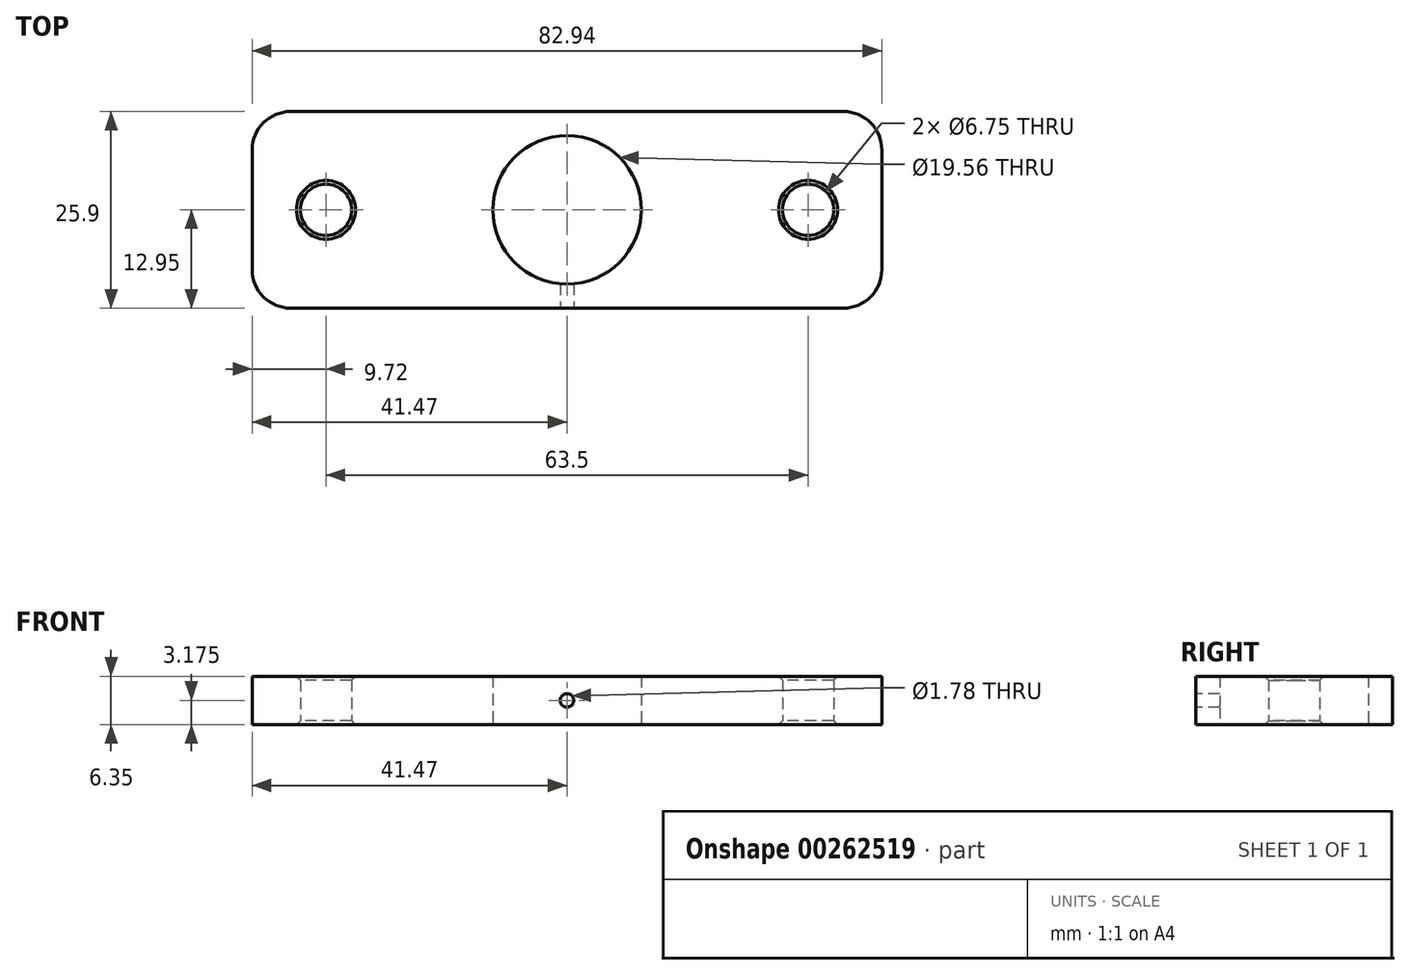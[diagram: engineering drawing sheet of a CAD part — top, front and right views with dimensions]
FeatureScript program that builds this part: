
annotation { "Feature Type Name" : "Feature", "Feature Type Description" : "" }
export const myFeature = defineFeature(function(context is Context, id is Id, definition is map)
    precondition{}
    {
        {
            var Q0;
            Q0=qCreatedBy(makeId("Top.planeOp"),FACE);
            var sketch = newSketch(context, id + "F0", { "sketchPlane" : qUnion([Q0])});
            skLineSegment(sketch, "E0.bottom", {"start": v(-41.47, 12.95) * mm, "end": v(41.47, 12.95) * mm});
            skLineSegment(sketch, "E0.top", {"start": v(-41.47, -12.95) * mm, "end": v(41.47, -12.95) * mm});
            skLineSegment(sketch, "E0.left", {"start": v(-41.47, 12.95) * mm, "end": v(-41.47, -12.95) * mm});
            skLineSegment(sketch, "E0.right", {"start": v(41.47, 12.95) * mm, "end": v(41.47, -12.95) * mm});
            skPoint(sketch, "E0.middle", {"position": v(0, 0) * mm});
            skCircle(sketch, "E1", {"center": v(0, 0) * mm, "radius": 9.78 * mm});
            skCircle(sketch, "E2", {"center": v(-31.75, 0) * mm, "radius": 3.37 * mm});
            skCircle(sketch, "E3", {"center": v(31.75, 0) * mm, "radius": 3.37 * mm});
            skSolve(sketch);
        }
        {
            var Q0;
            Q0 = qSketchRegion(id + "F0", true);
            extrude(context, id + "F1", {"entities" : qUnion([Q0]), "depth" : 6.35 * mm});
        }
        {
            var Q0;
            Q0=makeQuery(id+"F1.opExtrude","SWEPT_FACE",FACE,{"disambiguationData":[OSD([sQuery(id+"F0.wireOp",EDGE,"E0.top")])]});
            var sketch = newSketch(context, id + "F2", { "sketchPlane" : qUnion([Q0])});
            skCircle(sketch, "E4", {"center": v(0, 3.18) * mm, "radius": 0.89 * mm});
            skLineSegment(sketch, "E5", {"start": v(0, 0) * mm, "end": v(0, 3.18) * mm, "construction": true});
            skLineSegment(sketch, "E6", {"start": v(0, 6.35) * mm, "end": v(0, 3.18) * mm, "construction": true});
            skSolve(sketch);
        }
        {
            var Q0;
            Q0 = qSketchRegion(id + "F2", true);
            extrude(context, id + "F3", {"entities" : qUnion([Q0]), "operationType" : NewBodyOperationType.REMOVE, "endBound" : BoundingType.UP_TO_NEXT, "oppositeDirection" : true, "depth" : 25.4 * mm});
        }
        {
            var Q0;
            Q0=makeQuery(id+"F1.opExtrude","SWEPT_EDGE",EDGE,{"disambiguationData":[OSD([sQuery(id+"F0.wireOp",EDGE,"E0.top"),sQuery(id+"F0.wireOp",EDGE,"E0.left")])]});
            var Q1;
            Q1=makeQuery(id+"F1.opExtrude","SWEPT_EDGE",EDGE,{"disambiguationData":[OSD([sQuery(id+"F0.wireOp",EDGE,"E0.top"),sQuery(id+"F0.wireOp",EDGE,"E0.right")])]});
            var Q2;
            Q2=makeQuery(id+"F1.opExtrude","SWEPT_EDGE",EDGE,{"disambiguationData":[OSD([sQuery(id+"F0.wireOp",EDGE,"E0.bottom"),sQuery(id+"F0.wireOp",EDGE,"E0.right")])]});
            var Q3;
            Q3=makeQuery(id+"F1.opExtrude","SWEPT_EDGE",EDGE,{"disambiguationData":[OSD([sQuery(id+"F0.wireOp",EDGE,"E0.bottom"),sQuery(id+"F0.wireOp",EDGE,"E0.left")])]});
            fillet(context, id + "F4", {"entities" : qUnion([Q0, Q1, Q2, Q3]), "radius" : 5.08 * mm, "tangentPropagation" : true, "allowEdgeOverflow" : false});
        }
        {
            var Q0;
            Q0=makeQuery(id+"F1.opExtrude","CAP_EDGE",EDGE,{"disambiguationData":[OSD([sQuery(id+"F0.wireOp",EDGE,"E2")])],"isStart":false});
            var Q1;
            Q1=makeQuery(id+"F1.opExtrude","CAP_EDGE",EDGE,{"disambiguationData":[OSD([sQuery(id+"F0.wireOp",EDGE,"E3")])],"isStart":false});
            var Q2;
            Q2=makeQuery(id+"F1.opExtrude","CAP_EDGE",EDGE,{"disambiguationData":[OSD([sQuery(id+"F0.wireOp",EDGE,"E2")])],"isStart":true});
            var Q3;
            Q3=makeQuery(id+"F1.opExtrude","CAP_EDGE",EDGE,{"disambiguationData":[OSD([sQuery(id+"F0.wireOp",EDGE,"E3")])],"isStart":true});
            chamfer(context, id + "F5", {"entities" : qUnion([Q0, Q1, Q2, Q3]), "width" : 0.5 * mm, "tangentPropagation" : true});
        }
    });
